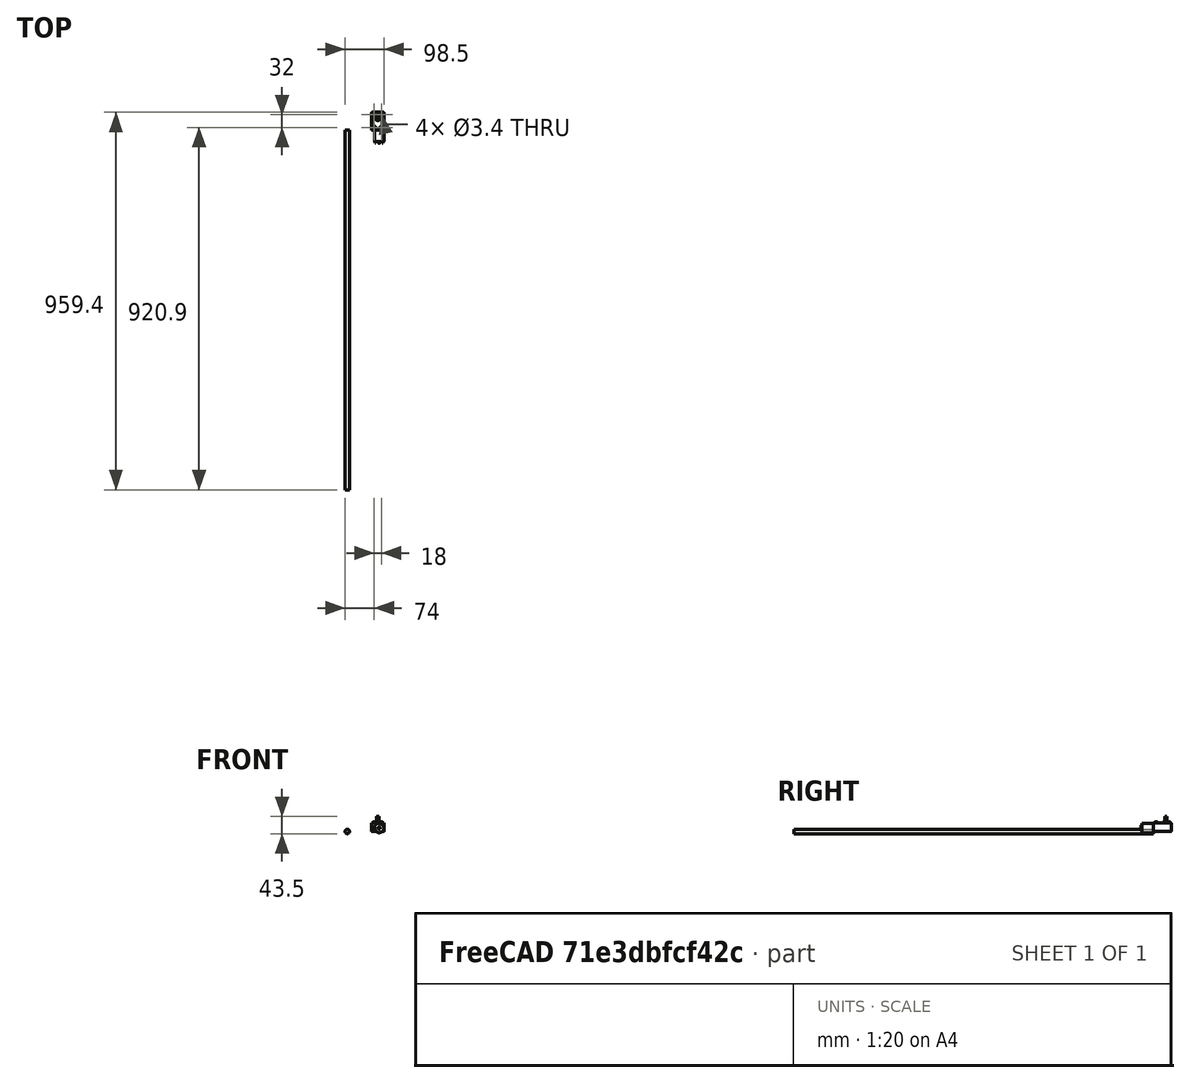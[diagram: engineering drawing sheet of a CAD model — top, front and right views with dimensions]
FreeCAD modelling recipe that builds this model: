
FCSTD DOCUMENT  (FreeCAD 1.1R20260414 (Git shallow))
Label: chainsword_master
License: All rights reserved
LicenseURL: https://en.wikipedia.org/wiki/All_rights_reserved
objects: App::Link×13, Sketcher::SketchObject×7, PartDesign::Pad×6, App::Point×5, PartDesign::Fillet×3, PartDesign::Body×2, App::FeaturePython×2, Assembly::AssemblyLink×2, PartDesign::Hole×1, PartDesign::Pocket×1, Assembly::JointGroup×1, Assembly::AssemblyObject×1
note: 49 computed .brp shape members not serialized (recipe doc carries the construction recipe); baked Part::Feature solids carry a one-line shape summary decoded from their .brp
EXTERNAL_REF file=../eletronic_parts/12v_battery.FCStd obj=Body
EXTERNAL_REF file=../eletronic_parts/spring_button.FCStd obj=Assembly
EXTERNAL_REF file=../eletronic_parts/spring_button.FCStd obj=base
EXTERNAL_REF file=../eletronic_parts/spring_button.FCStd obj=pins
EXTERNAL_REF file=../eletronic_parts/spring_button.FCStd obj=nut
EXTERNAL_REF file=../eletronic_parts/spring_button.FCStd obj=button
EXTERNAL_REF file=../eletronic_parts/dc_to_2wire.FCStd obj=Assembly
EXTERNAL_REF file=../eletronic_parts/dc_to_2wire.FCStd obj=base
EXTERNAL_REF file=../eletronic_parts/dc_to_2wire.FCStd obj=connectors
EXTERNAL_REF file=../eletronic_parts/dc_to_2wire.FCStd obj=sockets
EXTERNAL_REF file=../eletronic_parts/dc_to_2wire.FCStd obj=aux
EXTERNAL_REF file=housing.FCStd obj=Body001

FEATURE [App::Point] Origin001
  Role = Origin
FEATURE [App::Point] Origin003
  Role = Origin
FEATURE [Sketcher::SketchObject] Sketch
  ArcFitTolerance = 1e-06
  AttachmentSupport = -> [Origin002]
  ExternalTypes = [0]
  FullyConstrained = true
  MakeInternals = false
  MapMode = 5
  Placement = pos=(0,0,0) rot=(1,0,0;1.5708rad)
  _ExternalGeoVersion = 1
  sketch-geometry (1):
    g0: Circle CenterX=0 CenterY=0 CenterZ=0 NormalX=0 NormalY=0 NormalZ=1 AngleXU=0 Radius=5.5
  constraints (2):
    c: Diameter(g0) = 11
    c: Coincident(g0,g-1)
FEATURE [PartDesign::Pad] Pad
  Direction = (0,-1,2e-16)
  Length = 914.4
  Length2 = 10
  Profile = -> Sketch
  ReferenceAxis = -> Sketch [N_Axis]
  Refine = true
  SideType = 0
  Suppressed = false
  Type = 0
  Type2 = 0
FEATURE [PartDesign::Body] Body  label="threaded_rod"
  AllowCompound = false
  Group = -> [Sketch,Pad]
  Origin = -> Origin002
  Placement = pos=(133,0,0) rot=(0,0,1;0rad)
  Tip = -> Pad
FEATURE [App::Point] Origin005  label="Origin006"
  Role = Origin
FEATURE [Sketcher::SketchObject] Sketch001
  ArcFitTolerance = 1e-06
  AttachmentSupport = -> [Origin004]
  ExternalTypes = [0]
  FullyConstrained = true
  MakeInternals = false
  MapMode = 5
  _ExternalGeoVersion = 1
  sketch-geometry (4):
    g0: LineSegment StartX=0 StartY=0 StartZ=0 EndX=31 EndY=0 EndZ=0
    g1: LineSegment StartX=31 StartY=0 StartZ=0 EndX=31 EndY=45 EndZ=0
    g2: LineSegment StartX=31 StartY=45 StartZ=0 EndX=0 EndY=45 EndZ=0
    g3: LineSegment StartX=0 StartY=45 StartZ=0 EndX=0 EndY=0 EndZ=0
  constraints (11):
    c: Coincident(g0,g1)
    c: Coincident(g1,g2)
    c: Coincident(g2,g3)
    c: Coincident(g3,g0)
    c: Horizontal(g0)
    c: Horizontal(g2)
    c: Vertical(g1)
    c: Vertical(g3)
    c: Distance(g1,g3) = 31
    c: Distance(g0,g2) = 45
    c: Coincident(g0,g-1)
FEATURE [PartDesign::Pad] Pad001
  Direction = (0,0,1)
  Length = 22
  Length2 = 10
  Profile = -> Sketch001
  ReferenceAxis = -> Sketch001 [N_Axis]
  Refine = true
  SideType = 0
  Suppressed = false
  Type = 0
  Type2 = 0
FEATURE [Sketcher::SketchObject] Sketch002
  ArcFitTolerance = 1e-06
  AttachmentSupport = -> [Pad001]
  ExternalGeometry = -> [Pad001]
  ExternalTypes = [0]
  FullyConstrained = true
  MakeInternals = false
  MapMode = 5
  Placement = pos=(0,0,0) rot=(1,0,0;1.5708rad)
  _ExternalGeoVersion = 1
  sketch-geometry (1):
    g0: Circle CenterX=19 CenterY=9 CenterZ=0 NormalX=0 NormalY=0 NormalZ=1 AngleXU=0 Radius=12
  constraints (3):
    c: Diameter(g0) = 24
    c: Distance(g0,g-1) = 3
    c: Tangent(g0,g-3)
FEATURE [PartDesign::Pad] Pad002
  BaseFeature = -> Pad001
  Direction = (0,-1,2e-16)
  Length = 30
  Length2 = 10
  Profile = -> Sketch002 [Edge1]
  ReferenceAxis = -> Sketch002 [N_Axis]
  Refine = true
  SideType = 0
  Suppressed = false
  Type = 0
  Type2 = 0
FEATURE [Sketcher::SketchObject] Sketch003
  ArcFitTolerance = 1e-06
  AttachmentSupport = -> [Pad002]
  ExternalGeometry = -> [Pad002]
  ExternalTypes = [0]
  FullyConstrained = false
  MakeInternals = false
  MapMode = 5
  Placement = pos=(0,-30,0) rot=(1,0,0;1.5708rad)
  _ExternalGeoVersion = 1
  sketch-geometry (9):
    g0: LineSegment StartX=26.7462 StartY=15.1042 StartZ=0 EndX=28.7462 EndY=15.1042 EndZ=0
    g1: LineSegment StartX=28.7462 StartY=15.1042 StartZ=0 EndX=28.7462 EndY=14.9042 EndZ=0
    g2: LineSegment StartX=28.7462 StartY=14.9042 StartZ=0 EndX=26.7462 EndY=14.9042 EndZ=0
    g3: LineSegment StartX=26.7462 StartY=14.9042 StartZ=0 EndX=26.7462 EndY=15.1042 EndZ=0
    g4: LineSegment StartX=8.30695 StartY=4.56812 StartZ=0 EndX=10.307 EndY=4.56812 EndZ=0
    g5: LineSegment StartX=10.307 StartY=4.56812 StartZ=0 EndX=10.307 EndY=4.76812 EndZ=0
    g6: LineSegment StartX=10.307 StartY=4.76812 StartZ=0 EndX=8.30695 EndY=4.76812 EndZ=0
    g7: LineSegment StartX=8.30695 StartY=4.76812 StartZ=0 EndX=8.30695 EndY=4.56812 EndZ=0
    g8: Circle CenterX=19 CenterY=9 CenterZ=0 NormalX=0 NormalY=0 NormalZ=1 AngleXU=0 Radius=2.5
  constraints (24):
    c: Coincident(g0,g1)
    c: Coincident(g1,g2)
    c: Coincident(g2,g3)
    c: Coincident(g3,g0)
    c: Horizontal(g0)
    c: Horizontal(g2)
    c: Vertical(g1)
    c: Vertical(g3)
    c: Coincident(g4,g5)
    c: Coincident(g5,g6)
    c: Coincident(g6,g7)
    c: Coincident(g7,g4)
    c: Horizontal(g4)
    c: Horizontal(g6)
    c: Vertical(g5)
    c: Vertical(g7)
    c: Distance(g5,g7) = 2
    c: Distance(g4,g6) = 0.2
    c: Equal(g2,g6)
    c: Equal(g7,g3)
    c: Distance(g6,g-3) = 0.5
    c: Distance(g0,g-3) = 0.5
    c: Coincident(g8,g-3)
    c: Diameter(g8) = 5
FEATURE [PartDesign::Pad] Pad003
  BaseFeature = -> Pad002
  Direction = (0,-1,2e-16)
  Length = 3
  Length2 = 10
  Profile = -> Sketch003
  ReferenceAxis = -> Sketch003 [N_Axis]
  Refine = true
  SideType = 0
  Suppressed = false
  Type = 0
  Type2 = 0
FEATURE [PartDesign::Fillet] Fillet
  Base = -> Pad003 [Edge39]
  BaseFeature = -> Pad003
  Radius = 0.1
  Refine = true
  SupportTransform = false
  Suppressed = false
  UseAllEdges = false
FEATURE [PartDesign::Fillet] Fillet001
  Base = -> Fillet [Edge42,Edge43,Edge44,Edge40,Edge35,Edge38,Edge49,Edge45]
  BaseFeature = -> Fillet
  Radius = 1
  Refine = true
  SupportTransform = false
  Suppressed = false
  UseAllEdges = false
FEATURE [Sketcher::SketchObject] Sketch004
  ArcFitTolerance = 1e-06
  AttachmentSupport = -> [Fillet001]
  ExternalGeometry = -> [Fillet001]
  ExternalTypes = [0,0]
  FullyConstrained = true
  MakeInternals = false
  MapMode = 5
  Placement = pos=(0,0,22) rot=(0,0,1;0rad)
  _ExternalGeoVersion = 1
  sketch-geometry (5):
    g0: Circle CenterX=6.5 CenterY=6.5 CenterZ=0 NormalX=0 NormalY=0 NormalZ=1 AngleXU=0 Radius=3.5
    g1: Circle CenterX=6.5 CenterY=38.5 CenterZ=0 NormalX=0 NormalY=0 NormalZ=1 AngleXU=0 Radius=3.5
    g2: Circle CenterX=24.5 CenterY=6.5 CenterZ=0 NormalX=0 NormalY=0 NormalZ=1 AngleXU=0 Radius=3.5
    g3: Circle CenterX=24.5 CenterY=38.5 CenterZ=0 NormalX=0 NormalY=0 NormalZ=1 AngleXU=0 Radius=3.5
    g4: Circle CenterX=15.5 CenterY=30.5 CenterZ=0 NormalX=0 NormalY=0 NormalZ=1 AngleXU=0 Radius=6.5
  constraints (15):
    c: Diameter(g0) = 7
    c: Distance(g0,g-2) = 3
    c: Distance(g0,g-1) = 3
    c: Equal(g0,g1)
    c: Equal(g0,g2)
    c: Equal(g0,g3)
    c: Distance(g1,g-3) = 3
    c: Distance(g1,g-2) = 3
    c: Distance(g3,g-3) = 3
    c: Distance(g3,g-4) = 3
    c: Distance(g2,g-4) = 3
    c: Distance(g2,g-1) = 3
    c: Diameter(g4) = 13
    c: Distance(g4,g-3) = 8
    c: Distance(g4,g-2) = 9
FEATURE [PartDesign::Pad] Pad004
  BaseFeature = -> Fillet001
  Direction = (0,0,1)
  Length = 2
  Length2 = 10
  Profile = -> Sketch004
  ReferenceAxis = -> Sketch004 [N_Axis]
  Refine = true
  SideType = 0
  Suppressed = false
  Type = 0
  Type2 = 0
FEATURE [PartDesign::Hole] Hole
  BaseFeature = -> Pad004
  BaseProfileType = 7
  CustomThreadClearance = 0
  Depth = 3
  DepthType = 0
  Diameter = 3.4
  DrillForDepth = false
  DrillPoint = 1
  DrillPointAngle = 118
  HoleCutCountersinkAngle = 90
  HoleCutCustomValues = false
  HoleCutDepth = 0
  HoleCutDiameter = 0
  HoleCutType = 0
  ModelThread = false
  Profile = -> Pad004 [Face43,Face41,Face39,Face40]
  Refine = true
  Suppressed = false
  Tapered = false
  TaperedAngle = 90
  ThreadClass = 0
  ThreadDepth = 3
  ThreadDepthType = 0
  ThreadDiameter = 3
  ThreadDirection = 0
  ThreadFit = 0
  ThreadSize = 9
  ThreadType = 1
  Threaded = false
  UseCustomThreadClearance = false
FEATURE [PartDesign::Fillet] Fillet002
  Base = -> Hole [Edge80,Edge84,Edge88,Edge82,Edge86]
  BaseFeature = -> Hole
  Radius = 0.2
  Refine = true
  SupportTransform = false
  Suppressed = false
  UseAllEdges = false
FEATURE [Sketcher::SketchObject] Sketch005
  ArcFitTolerance = 1e-06
  AttachmentSupport = -> [Fillet002]
  ExternalGeometry = -> [Fillet002]
  ExternalTypes = [0]
  FullyConstrained = true
  MakeInternals = false
  MapMode = 5
  Placement = pos=(0,0,24) rot=(0,0,1;0rad)
  _ExternalGeoVersion = 1
  sketch-geometry (1):
    g0: Circle CenterX=15.5 CenterY=30.5 CenterZ=0 NormalX=0 NormalY=0 NormalZ=1 AngleXU=0 Radius=3
  constraints (2):
    c: Diameter(g0) = 6
    c: Coincident(g0,g-3)
FEATURE [PartDesign::Pad] Pad005
  BaseFeature = -> Fillet002
  Direction = (0,0,1)
  Length = 14
  Length2 = 10
  Profile = -> Sketch005
  ReferenceAxis = -> Sketch005 [N_Axis]
  Refine = true
  SideType = 0
  Suppressed = false
  Type = 0
  Type2 = 0
FEATURE [Sketcher::SketchObject] Sketch006
  ArcFitTolerance = 1e-06
  AttachmentSupport = -> [Pad005]
  ExternalGeometry = -> [Pad005]
  ExternalTypes = [0]
  FullyConstrained = false
  MakeInternals = false
  MapMode = 5
  Placement = pos=(0,0,38) rot=(0,0,1;0rad)
  _ExternalGeoVersion = 1
  sketch-geometry (4):
    g0: LineSegment StartX=14.0077 StartY=27.8975 StartZ=0 EndX=14.0077 EndY=27.0465 EndZ=0
    g1: LineSegment StartX=14.0077 StartY=27.0465 StartZ=0 EndX=17.0077 EndY=27.0465 EndZ=0
    g2: LineSegment StartX=17.0077 StartY=27.0465 StartZ=0 EndX=17.0077 EndY=27.8975 EndZ=0
    g3: LineSegment StartX=17.0077 StartY=27.8975 StartZ=0 EndX=14.0077 EndY=27.8975 EndZ=0
  constraints (10):
    c: Coincident(g0,g1)
    c: Coincident(g1,g2)
    c: Coincident(g2,g3)
    c: Coincident(g3,g0)
    c: Vertical(g0)
    c: Vertical(g2)
    c: Horizontal(g1)
    c: Horizontal(g3)
    c: PointOnObject(g0,g-3)
    c: DistanceX(g3,g3) = 3
FEATURE [PartDesign::Pocket] Pocket
  BaseFeature = -> Pad005
  Direction = (0,0,-1)
  Length = 12
  Length2 = 5
  Profile = -> Sketch006
  ReferenceAxis = -> Sketch006 [N_Axis]
  Refine = true
  SideType = 0
  Suppressed = false
  Type = 0
  Type2 = 0
FEATURE [PartDesign::Body] Body001  label="12v_DC_Motor"
  AllowCompound = true
  Group = -> [Sketch001,Pad001,Sketch002,Pad002,Sketch003,Pad003,Fillet,Fillet001,Sketch004,Pad004,Hole,Fillet002,Sketch005,Pad005,Sketch006,Pocket]
  Origin = -> Origin004
  Placement = pos=(195,0,0) rot=(0,0,1;0rad)
  Tip = -> Pocket
FEATURE [App::Link] Link
FEATURE [App::Link] threaded_rod  label="threaded_rod001"
  LinkedObject = -> Body
FEATURE [App::FeaturePython] GroundedJoint  # Assembly grounded joint (typed FeaturePython)
  ObjectToGround = -> threaded_rod
FEATURE [App::Link] _12v_DC_Motor  label="12v_DC_Motor001"
  LinkPlacement = pos=(34.2445,-236.883,-25.2543) rot=(-0.603023,-0.603023,0.603023;2.0944rad)
  LinkedObject = -> Body001
  Placement = pos=(34.2445,-236.883,-25.2543) rot=(-0.603023,-0.603023,0.603023;2.0944rad)
FEATURE [App::Link] Body002  label="Body"
  LinkPlacement = pos=(-22.0557,-193.633,-86.7561) rot=(0,0,1.04447;3.53429rad)
  LinkedObject = -> <external ../eletronic_parts/12v_battery.FCStd>#Body
  Placement = pos=(-22.0557,-193.633,-86.7561) rot=(0,0,1.04447;3.53429rad)
FEATURE [App::Point] Origin009  label="Origin011"
  Role = Origin
FEATURE [App::Link] base001  label="base002"
  LinkedObject = -> <external ../eletronic_parts/spring_button.FCStd>#base
FEATURE [App::Link] pins001  label="pins002"
  LinkPlacement = pos=(-0.25,7e-16,1) rot=(0,0,1;0rad)
  LinkedObject = -> <external ../eletronic_parts/spring_button.FCStd>#pins
  Placement = pos=(-0.25,7e-16,1) rot=(0,0,1;0rad)
FEATURE [App::Link] nut001  label="nut002"
  LinkPlacement = pos=(0,-11.7053,2.6e-15) rot=(0,0,1;0rad)
  LinkedObject = -> <external ../eletronic_parts/spring_button.FCStd>#nut
  Placement = pos=(0,-11.7053,2.6e-15) rot=(0,0,1;0rad)
FEATURE [App::Link] button001  label="button002"
  LinkPlacement = pos=(-4.8e-15,1.5,-4.6e-15) rot=(0,1,0;1.5708rad)
  LinkedObject = -> <external ../eletronic_parts/spring_button.FCStd>#button
  Placement = pos=(-4.8e-15,1.5,-4.6e-15) rot=(0,1,0;1.5708rad)
FEATURE [Assembly::AssemblyLink] Assembly002  label="button"
  Group = -> [base001,pins001,nut001,button001]
  LinkedObject = -> <external ../eletronic_parts/spring_button.FCStd>#Assembly
  Origin = -> Origin008
  Placement = pos=(-23.2078,-199.6,-0.0785183) rot=(0.999349,0,0;1.5708rad)
  Rigid = true
FEATURE [App::Point] Origin011  label="Origin013"
  Role = Origin
FEATURE [App::Link] base  label="base001"
  LinkedObject = -> <external ../eletronic_parts/dc_to_2wire.FCStd>#base
FEATURE [App::Link] connectors  label="connectors001"
  LinkPlacement = pos=(1,1,1) rot=(0,0,1;0rad)
  LinkedObject = -> <external ../eletronic_parts/dc_to_2wire.FCStd>#connectors
  Placement = pos=(1,1,1) rot=(0,0,1;0rad)
FEATURE [App::Link] sockets  label="sockets001"
  LinkPlacement = pos=(1,1,1) rot=(0,0,1;0rad)
  LinkedObject = -> <external ../eletronic_parts/dc_to_2wire.FCStd>#sockets
  Placement = pos=(1,1,1) rot=(0,0,1;0rad)
FEATURE [App::Link] aux  label="aux001"
  LinkPlacement = pos=(4e-16,-3.6e-15,-1.1e-15) rot=(0,0,1;0rad)
  LinkedObject = -> <external ../eletronic_parts/dc_to_2wire.FCStd>#aux
  Placement = pos=(4e-16,-3.6e-15,-1.1e-15) rot=(0,0,1;0rad)
FEATURE [Assembly::AssemblyLink] Assembly003  label="connector"
  Group = -> [base,connectors,sockets,aux]
  LinkedObject = -> <external ../eletronic_parts/dc_to_2wire.FCStd>#Assembly
  Origin = -> Origin010
  Placement = pos=(19.7616,-220.699,42.4752) rot=(-1.04447,0,0;1.5708rad)
  Rigid = true
FEATURE [App::Link] Body003  label="housing"
  LinkPlacement = pos=(-4.9e-15,-129.382,-39.75) rot=(0,0,1;0rad)
  LinkedObject = -> <external housing.FCStd>#Body001
  Placement = pos=(-4.9e-15,-129.382,-39.75) rot=(0,0,1;0rad)
FEATURE [App::FeaturePython] Joint  label="Slider001"  # Assembly joint (typed FeaturePython)
  Angle = 0
  AngleMax = 0
  AngleMin = 0
  Detach1 = false
  Detach2 = false
  Distance = 0
  Distance2 = 0
  EnableAngleMax = false
  EnableAngleMin = false
  EnableLengthMax = false
  EnableLengthMin = false
  JointType = 3 (Slider)
  LengthMax = 0
  LengthMin = 0
  Offset2 = pos=(0,0,0) rot=(0,0,1;3.14159rad)
  Placement1 = pos=(40,-61,-55) rot=(1,0,0;1.5708rad)
  Placement2 = pos=(0,0,0) rot=(0,-0.707107,0.707107;3.14159rad)
  Reference1 = -> Body003 [?Face20,?Face20]
  Reference2 = -> threaded_rod [Face1,Edge2]
  Suppressed = false
FEATURE [Assembly::JointGroup] Joints
  Group = -> [GroundedJoint,Joint]
FEATURE [Assembly::AssemblyObject] Assembly
  Group = -> [Joints,Link,threaded_rod,GroundedJoint,_12v_DC_Motor,Body002,Assembly002,Assembly003,Body003,Joint]
  Origin = -> Origin
  Type = Assembly

RESOLVED EXTERNAL PARTS (link-assembly join: the EXTERNAL_REF files above that resolve inside this repo's crawl, each included once):
---- part ../eletronic_parts/12v_battery.FCStd = doc fcstd_0e6d6dc54b79 ----
FCSTD DOCUMENT  (FreeCAD 1.1R20260414 (Git shallow))
Label: 12v_battery
License: All rights reserved
LicenseURL: https://en.wikipedia.org/wiki/All_rights_reserved
objects: Sketcher::SketchObject×2, PartDesign::Pad×2, App::Point×1, PartDesign::Fillet×1, PartDesign::Body×1
note: 14 computed .brp shape members not serialized (recipe doc carries the construction recipe); baked Part::Feature solids carry a one-line shape summary decoded from their .brp

FEATURE [App::Point] Origin001
  Role = Origin
FEATURE [Sketcher::SketchObject] Sketch
  ArcFitTolerance = 1e-06
  AttachmentSupport = -> [Origin]
  ExternalTypes = [0]
  FullyConstrained = true
  MakeInternals = false
  MapMode = 5
  _ExternalGeoVersion = 1
  sketch-geometry (4):
    g0: LineSegment StartX=23.094 StartY=0 StartZ=0 EndX=-11.547 EndY=20 EndZ=0
    g1: LineSegment StartX=-11.547 StartY=20 StartZ=0 EndX=-11.547 EndY=-20 EndZ=0
    g2: LineSegment StartX=-11.547 StartY=-20 StartZ=0 EndX=23.094 EndY=0 EndZ=0
    g3: Circle [constr] CenterX=0 CenterY=0 CenterZ=0 NormalX=0 NormalY=0 NormalZ=1 AngleXU=0 Radius=23.094
  constraints (11):
    c: Coincident(g0,g1)
    c: Coincident(g1,g2)
    c: Coincident(g2,g0)
    c: Equal(g0,g1)
    c: Equal(g0,g2)
    c: PointOnObject(g0,g3)
    c: PointOnObject(g1,g3)
    c: PointOnObject(g2,g3)
    c: Coincident(g3,g-1)
    c: PointOnObject(g2,g-1)
    c: Distance(g0,g0) = 40
FEATURE [PartDesign::Pad] Pad
  Direction = (0,0,1)
  Length = 62
  Length2 = 10
  Profile = -> Sketch
  ReferenceAxis = -> Sketch [N_Axis]
  Refine = true
  SideType = 0
  Suppressed = false
  Type = 0
  Type2 = 0
FEATURE [PartDesign::Fillet] Fillet
  Base = -> Pad [Edge2,Edge1,Edge5]
  BaseFeature = -> Pad
  Radius = 1
  Refine = true
  SupportTransform = false
  Suppressed = false
  UseAllEdges = false
FEATURE [Sketcher::SketchObject] Sketch001
  ArcFitTolerance = 1e-06
  AttachmentSupport = -> [Fillet]
  ExternalGeometry = -> [Fillet]
  ExternalTypes = [0]
  FullyConstrained = true
  MakeInternals = false
  MapMode = 5
  Placement = pos=(0,0,62) rot=(0,0,1;0rad)
  _ExternalGeoVersion = 1
  sketch-geometry (4):
    g0: LineSegment StartX=-11.547 StartY=5.5 StartZ=0 EndX=-11.547 EndY=-5.5 EndZ=0
    g1: LineSegment StartX=-11.547 StartY=-5.5 StartZ=0 EndX=-1.54701 EndY=-5.5 EndZ=0
    g2: LineSegment StartX=-1.54701 StartY=-5.5 StartZ=0 EndX=-1.54701 EndY=5.5 EndZ=0
    g3: LineSegment StartX=-1.54701 StartY=5.5 StartZ=0 EndX=-11.547 EndY=5.5 EndZ=0
  constraints (12):
    c: Coincident(g0,g1)
    c: Coincident(g1,g2)
    c: Coincident(g2,g3)
    c: Coincident(g3,g0)
    c: Vertical(g0)
    c: Vertical(g2)
    c: Horizontal(g1)
    c: Horizontal(g3)
    c: PointOnObject(g0,g-3)
    c: DistanceX(g3,g3) = 10
    c: DistanceY(g0,g0) = 11
    c: Distance(g-1,g3) = 5.5
FEATURE [PartDesign::Pad] Pad001
  BaseFeature = -> Fillet
  Direction = (0,0,1)
  Length = 5
  Length2 = 10
  Profile = -> Sketch001
  ReferenceAxis = -> Sketch001 [N_Axis]
  Refine = true
  SideType = 0
  Suppressed = false
  Type = 0
  Type2 = 0
FEATURE [PartDesign::Body] Body
  AllowCompound = true
  Group = -> [Sketch,Pad,Fillet,Sketch001,Pad001]
  Origin = -> Origin
  Tip = -> Pad001
---- part ../eletronic_parts/dc_to_2wire.FCStd = doc fcstd_c95eb83013e7 ----
FCSTD DOCUMENT  (FreeCAD 1.1R20260414 (Git shallow))
Label: dc_to_2wire
License: All rights reserved
LicenseURL: https://en.wikipedia.org/wiki/All_rights_reserved
objects: Sketcher::SketchObject×9, PartDesign::Pad×7, App::Point×5, PartDesign::Plane×5, PartDesign::Body×4, App::Link×4, App::FeaturePython×4, PartDesign::Fillet×2, PartDesign::Mirrored×2, PartDesign::AdditiveLoft×1, PartDesign::SubtractivePipe×1, Assembly::JointGroup×1, Assembly::AssemblyObject×1
note: 64 computed .brp shape members not serialized (recipe doc carries the construction recipe); baked Part::Feature solids carry a one-line shape summary decoded from their .brp

FEATURE [App::Point] Origin001
  Role = Origin
FEATURE [Sketcher::SketchObject] Sketch
  ArcFitTolerance = 1e-06
  AttachmentSupport = -> [Origin]
  ExternalTypes = [0]
  FullyConstrained = true
  MakeInternals = false
  MapMode = 5
  Placement = pos=(0,0,0) rot=(1,0,0;1.5708rad)
  _ExternalGeoVersion = 1
  sketch-geometry (10):
    g0: LineSegment StartX=-6 StartY=-6 StartZ=0 EndX=6 EndY=-6 EndZ=0
    g1: LineSegment StartX=7 StartY=-5 StartZ=0 EndX=7 EndY=5 EndZ=0
    g2: LineSegment StartX=6 StartY=6 StartZ=0 EndX=-6 EndY=6 EndZ=0
    g3: LineSegment StartX=-7 StartY=5 StartZ=0 EndX=-7 EndY=-5 EndZ=0
    g4: ArcOfCircle CenterX=-6 CenterY=-5 CenterZ=0 NormalX=0 NormalY=0 NormalZ=1 AngleXU=0 Radius=1 StartAngle=3.14159 EndAngle=4.71239
    g5: ArcOfCircle CenterX=6 CenterY=-5 CenterZ=0 NormalX=0 NormalY=0 NormalZ=1 AngleXU=0 Radius=1 StartAngle=4.71239 EndAngle=6.28319
    g6: ArcOfCircle CenterX=6 CenterY=5 CenterZ=0 NormalX=0 NormalY=0 NormalZ=1 AngleXU=0 Radius=1 StartAngle=0 EndAngle=1.5708
    g7: ArcOfCircle CenterX=-6 CenterY=5 CenterZ=0 NormalX=0 NormalY=0 NormalZ=1 AngleXU=0 Radius=1 StartAngle=1.5708 EndAngle=3.14159
    g8: GeomPoint [constr] X=7 Y=6 Z=0
    g9: GeomPoint [constr] X=-2.33e-14 Y=2.6e-14 Z=0
  constraints (22):
    c: Tangent(g0,g4) = -1.5708
    c: Tangent(g0,g5) = -1.5708
    c: Tangent(g1,g5) = -1.5708
    c: Tangent(g1,g6) = -1.5708
    c: Tangent(g2,g6) = -1.5708
    c: Tangent(g2,g7) = -1.5708
    c: Tangent(g3,g7) = -1.5708
    c: Tangent(g3,g4) = -1.5708
    c: Horizontal(g0)
    c: Horizontal(g2)
    c: Vertical(g1)
    c: Vertical(g3)
    c: Equal(g4,g5)
    c: Equal(g5,g6)
    c: Equal(g6,g7)
    c: Symmetric(g2,g0,g9)
    c: PointOnObject(g8,g1)
    c: PointOnObject(g8,g2)
    c: Distance(g1,g3) = 14
    c: Distance(g0,g2) = 12
    c: Radius(g5) = 1
    c: Coincident(g9,g-1)
FEATURE [PartDesign::Pad] Pad
  Direction = (0,-1,2e-16)
  Length = 12
  Length2 = 10
  Profile = -> Sketch
  ReferenceAxis = -> Sketch [N_Axis]
  Refine = true
  SideType = 0
  Suppressed = false
  Type = 0
  Type2 = 0
FEATURE [PartDesign::Plane] DatumPlane
  AttachmentOffset = pos=(0,0,10) rot=(0,0,1;0rad)
  AttachmentSupport = -> [Pad]
  Length = 60
  MapMode = 5
  Placement = pos=(0,-22,2.2e-15) rot=(1,0,0;1.5708rad)
  ResizeMode = 0
  Width = 60
FEATURE [Sketcher::SketchObject] Sketch001
  ArcFitTolerance = 1e-06
  AttachmentSupport = -> [DatumPlane]
  ExternalTypes = [0]
  FullyConstrained = true
  MakeInternals = false
  MapMode = 5
  Placement = pos=(0,-22,2.2e-15) rot=(1,0,0;1.5708rad)
  _ExternalGeoVersion = 1
  sketch-geometry (10):
    g0: LineSegment StartX=-5 StartY=-5.5 StartZ=0 EndX=5 EndY=-5.5 EndZ=0
    g1: LineSegment StartX=6 StartY=-4.5 StartZ=0 EndX=6 EndY=4.5 EndZ=0
    g2: LineSegment StartX=5 StartY=5.5 StartZ=0 EndX=-5 EndY=5.5 EndZ=0
    g3: LineSegment StartX=-6 StartY=4.5 StartZ=0 EndX=-6 EndY=-4.5 EndZ=0
    g4: ArcOfCircle CenterX=-5 CenterY=-4.5 CenterZ=0 NormalX=0 NormalY=0 NormalZ=1 AngleXU=0 Radius=1 StartAngle=3.14159 EndAngle=4.71239
    g5: ArcOfCircle CenterX=5 CenterY=-4.5 CenterZ=0 NormalX=0 NormalY=0 NormalZ=1 AngleXU=0 Radius=1 StartAngle=4.71239 EndAngle=6.28319
    g6: ArcOfCircle CenterX=5 CenterY=4.5 CenterZ=0 NormalX=0 NormalY=0 NormalZ=1 AngleXU=0 Radius=1 StartAngle=0 EndAngle=1.5708
    g7: ArcOfCircle CenterX=-5 CenterY=4.5 CenterZ=0 NormalX=0 NormalY=0 NormalZ=1 AngleXU=0 Radius=1 StartAngle=1.5708 EndAngle=3.14159
    g8: GeomPoint [constr] X=6 Y=5.5 Z=0
    g9: GeomPoint [constr] X=0 Y=1.17e-14 Z=0
  constraints (22):
    c: Tangent(g0,g4) = -1.5708
    c: Tangent(g0,g5) = -1.5708
    c: Tangent(g1,g5) = -1.5708
    c: Tangent(g1,g6) = -1.5708
    c: Tangent(g2,g6) = -1.5708
    c: Tangent(g2,g7) = -1.5708
    c: Tangent(g3,g7) = -1.5708
    c: Tangent(g3,g4) = -1.5708
    c: Horizontal(g0)
    c: Horizontal(g2)
    c: Vertical(g1)
    c: Vertical(g3)
    c: Equal(g4,g5)
    c: Equal(g5,g6)
    c: Equal(g6,g7)
    c: Symmetric(g2,g0,g9)
    c: PointOnObject(g8,g1)
    c: PointOnObject(g8,g2)
    c: Distance(g1,g3) = 12
    c: Distance(g0,g2) = 11
    c: Radius(g5) = 1
    c: Coincident(g9,g-1)
FEATURE [PartDesign::AdditiveLoft] AdditiveLoft
  BaseFeature = -> Pad
  Closed = false
  Profile = -> Pad [Face10]
  Refine = true
  Ruled = false
  Sections = -> [Sketch001]
  Suppressed = false
FEATURE [Sketcher::SketchObject] Sketch002
  ArcFitTolerance = 1e-06
  AttachmentSupport = -> [AdditiveLoft]
  ExternalTypes = [0]
  FullyConstrained = true
  MakeInternals = false
  MapMode = 5
  Placement = pos=(0,-22,0) rot=(1,0,0;1.5708rad)
  _ExternalGeoVersion = 1
  sketch-geometry (1):
    g0: Circle CenterX=0 CenterY=0 CenterZ=0 NormalX=0 NormalY=0 NormalZ=1 AngleXU=0 Radius=5
  constraints (2):
    c: Diameter(g0) = 10
    c: Coincident(g0,g-1)
FEATURE [PartDesign::Pad] Pad001
  BaseFeature = -> AdditiveLoft
  Direction = (0,-1,2e-16)
  Length = 6
  Length2 = 10
  Profile = -> Sketch002
  ReferenceAxis = -> Sketch002 [N_Axis]
  Refine = true
  SideType = 0
  Suppressed = false
  Type = 0
  Type2 = 0
FEATURE [PartDesign::Fillet] Fillet
  Base = -> Pad001 [Edge55]
  BaseFeature = -> Pad001
  Radius = 1
  Refine = true
  SupportTransform = false
  Suppressed = false
  UseAllEdges = false
FEATURE [Sketcher::SketchObject] Sketch003
  ArcFitTolerance = 1e-06
  AttachmentSupport = -> [Origin]
  ExternalGeometry = -> [Fillet]
  ExternalTypes = [0]
  FullyConstrained = false
  MakeInternals = false
  MapMode = 5
  Placement = pos=(0,0,0) rot=(0.57735,0.57735,0.57735;2.0944rad)
  _ExternalGeoVersion = 1
  sketch-geometry (24):
    g0: LineSegment StartX=-13 StartY=6.5 StartZ=0 EndX=-14 EndY=6.5 EndZ=0
    g1: LineSegment StartX=-14 StartY=6.5 StartZ=0 EndX=-14 EndY=5.5 EndZ=0
    g2: LineSegment StartX=-14 StartY=5.5 StartZ=0 EndX=-13 EndY=5.5 EndZ=0
    g3: LineSegment StartX=-13 StartY=5.5 StartZ=0 EndX=-13 EndY=6.5 EndZ=0
    g4: LineSegment StartX=-14.4641 StartY=6.45747 StartZ=0 EndX=-15.4641 EndY=6.45747 EndZ=0
    g5: LineSegment StartX=-15.4641 StartY=6.45747 StartZ=0 EndX=-15.4641 EndY=5.3215 EndZ=0
    g6: LineSegment StartX=-15.4641 StartY=5.3215 StartZ=0 EndX=-14.4641 EndY=5.3215 EndZ=0
    g7: LineSegment StartX=-14.4641 StartY=5.3215 StartZ=0 EndX=-14.4641 EndY=6.45747 EndZ=0
    g8: LineSegment StartX=-15.9959 StartY=6.24299 StartZ=0 EndX=-16.9959 EndY=6.24299 EndZ=0
    g9: LineSegment StartX=-16.9959 StartY=6.24299 StartZ=0 EndX=-16.9959 EndY=5.24299 EndZ=0
    g10: LineSegment StartX=-16.9959 StartY=5.24299 StartZ=0 EndX=-15.9959 EndY=5.24299 EndZ=0
    g11: LineSegment StartX=-15.9959 StartY=5.24299 StartZ=0 EndX=-15.9959 EndY=6.24299 EndZ=0
    g12: LineSegment StartX=-17.4938 StartY=6.16449 StartZ=0 EndX=-18.4938 EndY=6.16449 EndZ=0
    g13: LineSegment StartX=-18.4938 StartY=6.16449 StartZ=0 EndX=-18.4938 EndY=5.16449 EndZ=0
    g14: LineSegment StartX=-18.4938 StartY=5.16449 StartZ=0 EndX=-17.4938 EndY=5.16449 EndZ=0
    g15: LineSegment StartX=-17.4938 StartY=5.16449 StartZ=0 EndX=-17.4938 EndY=6.16449 EndZ=0
    g16: LineSegment StartX=-18.9918 StartY=6.08598 StartZ=0 EndX=-19.9918 EndY=6.08598 EndZ=0
    g17: LineSegment StartX=-19.9918 StartY=6.08598 StartZ=0 EndX=-19.9918 EndY=5.08598 EndZ=0
    g18: LineSegment StartX=-19.9918 StartY=5.08598 StartZ=0 EndX=-18.9918 EndY=5.08598 EndZ=0
    g19: LineSegment StartX=-18.9918 StartY=5.08598 StartZ=0 EndX=-18.9918 EndY=6.08598 EndZ=0
    g20: LineSegment StartX=-20.4897 StartY=6.00748 StartZ=0 EndX=-21.4897 EndY=6.00748 EndZ=0
    g21: LineSegment StartX=-21.4897 StartY=6.00748 StartZ=0 EndX=-21.4897 EndY=5.00748 EndZ=0
    g22: LineSegment StartX=-21.4897 StartY=5.00748 StartZ=0 EndX=-20.4897 EndY=5.00748 EndZ=0
    g23: LineSegment StartX=-20.4897 StartY=5.00748 StartZ=0 EndX=-20.4897 EndY=6.00748 EndZ=0
  constraints (52):
    c: Coincident(g0,g1)
    c: Coincident(g1,g2)
    c: Coincident(g2,g3)
    c: Coincident(g3,g0)
    c: Horizontal(g0)
    c: Horizontal(g2)
    c: Vertical(g1)
    c: Vertical(g3)
    c: Distance(g1,g3) = 1
    c: Distance(g0,g2) = 1
    c: Distance(g-3,g3) = 1
    c: DistanceY(g-3,g0) = 0.5
    c: Coincident(g4,g5)
    c: Coincident(g8,g9)
    c: Coincident(g12,g13)
    c: Coincident(g16,g17)
    c: Coincident(g20,g21)
    c: Coincident(g5,g6)
    c: Coincident(g9,g10)
    c: Coincident(g13,g14)
    c: Coincident(g17,g18)
    c: Coincident(g21,g22)
    c: Coincident(g6,g7)
    c: Coincident(g10,g11)
    c: Coincident(g14,g15)
    c: Coincident(g18,g19)
    c: Coincident(g22,g23)
    c: Coincident(g7,g4)
    c: Coincident(g11,g8)
    c: Coincident(g15,g12)
    c: Coincident(g19,g16)
    c: Coincident(g23,g20)
    c: Horizontal(g4)
    c: Horizontal(g8)
    c: Horizontal(g12)
    c: Horizontal(g16)
    c: Horizontal(g20)
    c: Horizontal(g6)
    c: Horizontal(g10)
    c: Horizontal(g14)
    c: Horizontal(g18)
    c: Horizontal(g22)
    c: Vertical(g5)
    c: Vertical(g9)
    c: Vertical(g13)
    c: Vertical(g17)
    c: Vertical(g21)
    c: Vertical(g7)
    c: Vertical(g11)
    c: Vertical(g15)
    c: Vertical(g19)
    c: Vertical(g23)
FEATURE [PartDesign::SubtractivePipe] SubtractivePipe
  AuxiliaryCurvilinear = true
  AuxiliarySpineTangent = false
  BaseFeature = -> Fillet
  Binormal = (0,0,0)
  Mode = 0
  Profile = -> Sketch003
  Refine = true
  Spine = -> Fillet [Edge17,Edge16,Edge14,Edge12,Edge10,Edge8,Edge6,Edge7,Edge9,Edge11,Edge13,Edge15]
  SpineTangent = false
  Suppressed = false
  Transformation = 0
  Transition = 0
FEATURE [PartDesign::Body] Body  label="base"
  AllowCompound = true
  Group = -> [Sketch,Pad,DatumPlane,Sketch001,AdditiveLoft,Sketch002,Pad001,Fillet,Sketch003,SubtractivePipe]
  Origin = -> Origin
  Tip = -> SubtractivePipe
FEATURE [App::Point] Origin005  label="Origin006"
  Role = Origin
FEATURE [PartDesign::Plane] DatumPlane001
  Length = 60
  MapMode = 5
  Placement = pos=(0,1.3e-15,6) rot=(0,0,1;0rad)
  ResizeMode = 0
  Width = 60
FEATURE [Sketcher::SketchObject] Sketch006
  ArcFitTolerance = 1e-06
  AttachmentSupport = -> [DatumPlane001]
  ExternalTypes = [0]
  FullyConstrained = true
  MakeInternals = false
  MapMode = 5
  Placement = pos=(0,1.3e-15,6) rot=(0,0,1;0rad)
  _ExternalGeoVersion = 1
  sketch-geometry (5):
    g0: LineSegment StartX=-5 StartY=-2 StartZ=0 EndX=5 EndY=-2 EndZ=0
    g1: LineSegment StartX=5 StartY=-2 StartZ=0 EndX=5 EndY=3 EndZ=0
    g2: LineSegment StartX=5 StartY=3 StartZ=0 EndX=-5 EndY=3 EndZ=0
    g3: LineSegment StartX=-5 StartY=3 StartZ=0 EndX=-5 EndY=-2 EndZ=0
    g4: GeomPoint [constr] X=0 Y=0.5 Z=0
  constraints (13):
    c: Coincident(g0,g1)
    c: Coincident(g1,g2)
    c: Coincident(g2,g3)
    c: Coincident(g3,g0)
    c: Horizontal(g0)
    c: Horizontal(g2)
    c: Vertical(g1)
    c: Vertical(g3)
    c: Symmetric(g2,g0,g4)
    c: Distance(g1,g3) = 10
    c: Distance(g0,g2) = 5
    c: PointOnObject(g4,g-2)
    c: Distance(g-1,g0) = 2
FEATURE [PartDesign::Pad] Pad004
  Direction = (0,0,1)
  Length = 2
  Length2 = 10
  Placement = pos=(0,1.3e-15,6) rot=(0,0,1;0rad)
  Profile = -> Sketch006
  ReferenceAxis = -> Sketch006 [N_Axis]
  Refine = true
  SideType = 1
  Suppressed = false
  Type = 0
  Type2 = 0
FEATURE [PartDesign::Body] Body002  label="sockets"
  AllowCompound = true
  Group = -> [DatumPlane001,Sketch006,Pad004]
  Origin = -> Origin004
  Tip = -> Pad004
FEATURE [App::Point] Origin007  label="Origin009"
  Role = Origin
FEATURE [PartDesign::Plane] DatumPlane002
  AttachmentSupport = -> [Pad004]
  Length = 60
  MapMode = 5
  Placement = pos=(0,3,6) rot=(0,0.707107,0.707107;3.14159rad)
  ResizeMode = 0
  Width = 60
FEATURE [Sketcher::SketchObject] Sketch007
  ArcFitTolerance = 1e-06
  AttachmentSupport = -> [DatumPlane002]
  ExternalTypes = [0]
  FullyConstrained = true
  MakeInternals = false
  MapMode = 5
  Placement = pos=(0,3,6) rot=(0,0.707107,0.707107;3.14159rad)
  _ExternalGeoVersion = 1
  sketch-geometry (4):
    g0: LineSegment StartX=0.5 StartY=-4 StartZ=0 EndX=0.5 EndY=-9 EndZ=0
    g1: LineSegment StartX=0.5 StartY=-9 StartZ=0 EndX=4.5 EndY=-9 EndZ=0
    g2: LineSegment StartX=4.5 StartY=-9 StartZ=0 EndX=4.5 EndY=-4 EndZ=0
    g3: LineSegment StartX=4.5 StartY=-4 StartZ=0 EndX=0.5 EndY=-4 EndZ=0
  constraints (12):
    c: Coincident(g0,g1)
    c: Coincident(g1,g2)
    c: Coincident(g2,g3)
    c: Coincident(g3,g0)
    c: Vertical(g0)
    c: Vertical(g2)
    c: Horizontal(g1)
    c: Horizontal(g3)
    c: Distance(g0,g2) = 4
    c: Distance(g1,g3) = 5
    c: Distance(g-2,g0) = 0.5
    c: Distance(g-1,g3) = 4
FEATURE [PartDesign::Pad] Pad005
  Direction = (0,1,-2e-16)
  Length = 0.1
  Length2 = 10
  Placement = pos=(0,3,6) rot=(0,0.707107,0.707107;3.14159rad)
  Profile = -> Sketch007
  ReferenceAxis = -> Sketch007 [N_Axis]
  Refine = true
  SideType = 0
  Suppressed = false
  Type = 0
  Type2 = 0
FEATURE [PartDesign::Mirrored] Mirrored
  BaseFeature = -> Pad005
  MirrorPlane = -> Sketch007 [V_Axis]
  Originals = -> [Pad005]
  Placement = pos=(0,3,6) rot=(0,0.707107,0.707107;3.14159rad)
  Refine = true
  Suppressed = false
  TransformMode = 0
FEATURE [PartDesign::Plane] DatumPlane003
  AttachmentSupport = -> [Pad004]
  Length = 60
  MapMode = 5
  Placement = pos=(0,1.3e-15,8) rot=(0,0,1;0rad)
  ResizeMode = 0
  Width = 60
FEATURE [Sketcher::SketchObject] Sketch008
  ArcFitTolerance = 1e-06
  AttachmentSupport = -> [DatumPlane003]
  ExternalTypes = [0]
  FullyConstrained = true
  MakeInternals = false
  MapMode = 5
  Placement = pos=(0,1.3e-15,8) rot=(0,0,1;0rad)
  _ExternalGeoVersion = 1
  sketch-geometry (1):
    g0: Circle CenterX=-2.5 CenterY=1 CenterZ=0 NormalX=0 NormalY=0 NormalZ=1 AngleXU=0 Radius=1.5
  constraints (3):
    c: Diameter(g0) = 3
    c: Distance(g0,g-2) = 1
    c: Distance(g0,g-1) = 1
FEATURE [PartDesign::Pad] Pad006
  BaseFeature = -> Mirrored
  Direction = (0,0,1)
  Length = 0.1
  Length2 = 10
  Placement = pos=(0,3,6) rot=(0,0.707107,0.707107;3.14159rad)
  Profile = -> Sketch008
  ReferenceAxis = -> Sketch008 [N_Axis]
  Refine = true
  SideType = 0
  Suppressed = false
  Type = 0
  Type2 = 0
FEATURE [PartDesign::Mirrored] Mirrored001
  BaseFeature = -> Pad006
  MirrorPlane = -> Sketch008 [V_Axis]
  Originals = -> [Pad006]
  Placement = pos=(0,3,6) rot=(0,0.707107,0.707107;3.14159rad)
  Refine = true
  Suppressed = false
  TransformMode = 0
FEATURE [PartDesign::Body] Body003  label="connectors"
  AllowCompound = true
  Group = -> [DatumPlane002,Sketch007,Pad005,Mirrored,DatumPlane003,Sketch008,Pad006,Mirrored001]
  Origin = -> Origin006
  Tip = -> Mirrored001
FEATURE [App::Point] Origin009  label="Origin011"
  Role = Origin
FEATURE [PartDesign::Plane] DatumPlane004
  AttachmentSupport = -> [SubtractivePipe]
  Length = 60
  MapMode = 5
  Placement = pos=(0,-28,0) rot=(1,0,0;1.5708rad)
  ResizeMode = 0
  Width = 60
FEATURE [Sketcher::SketchObject] Sketch009
  ArcFitTolerance = 1e-06
  AttachmentSupport = -> [DatumPlane004]
  ExternalTypes = [0]
  FullyConstrained = true
  MakeInternals = false
  MapMode = 5
  Placement = pos=(0,-28,0) rot=(1,0,0;1.5708rad)
  _ExternalGeoVersion = 1
  sketch-geometry (2):
    g0: Circle CenterX=0 CenterY=0 CenterZ=0 NormalX=0 NormalY=0 NormalZ=1 AngleXU=0 Radius=3.5
    g1: Circle CenterX=0 CenterY=0 CenterZ=0 NormalX=0 NormalY=0 NormalZ=1 AngleXU=0 Radius=3.3
  constraints (4):
    c: Diameter(g0) = 7
    c: Coincident(g0,g-1)
    c: Coincident(g1,g0)
    c: Distance(g1,g0) = 0.2
FEATURE [PartDesign::Pad] Pad007
  Direction = (0,-1,2e-16)
  Length = 3
  Length2 = 10
  Placement = pos=(0,-28,0) rot=(1,0,0;1.5708rad)
  Profile = -> Sketch009
  ReferenceAxis = -> Sketch009 [N_Axis]
  Refine = true
  SideType = 0
  Suppressed = false
  TaperAngle = -4
  Type = 0
  Type2 = 0
FEATURE [Sketcher::SketchObject] Sketch010
  ArcFitTolerance = 1e-06
  AttachmentSupport = -> [DatumPlane004]
  ExternalTypes = [0]
  FullyConstrained = true
  MakeInternals = false
  MapMode = 5
  Placement = pos=(0,-28,0) rot=(1,0,0;1.5708rad)
  _ExternalGeoVersion = 1
  sketch-geometry (1):
    g0: Circle CenterX=0 CenterY=0 CenterZ=0 NormalX=0 NormalY=0 NormalZ=1 AngleXU=0 Radius=1
  constraints (2):
    c: Diameter(g0) = 2
    c: Coincident(g0,g-1)
FEATURE [PartDesign::Pad] Pad008
  BaseFeature = -> Pad007
  Direction = (0,-1,2e-16)
  Length = 2.5
  Length2 = 10
  Placement = pos=(0,-28,0) rot=(1,0,0;1.5708rad)
  Profile = -> Sketch010
  ReferenceAxis = -> Sketch010 [N_Axis]
  Refine = true
  SideType = 0
  Suppressed = false
  Type = 0
  Type2 = 0
FEATURE [PartDesign::Fillet] Fillet001
  Base = -> Pad008 [Edge9]
  BaseFeature = -> Pad008
  Placement = pos=(0,-28,0) rot=(1,0,0;1.5708rad)
  Radius = 1
  Refine = true
  SupportTransform = false
  Suppressed = false
  UseAllEdges = false
FEATURE [PartDesign::Body] Body004  label="aux"
  AllowCompound = true
  Group = -> [DatumPlane004,Sketch009,Pad007,Sketch010,Pad008,Fillet001]
  Origin = -> Origin008
  Tip = -> Fillet001
FEATURE [App::Point] Origin011  label="Origin014"
  Role = Origin
FEATURE [App::Link] base  label="base001"
  LinkedObject = -> Body
FEATURE [App::FeaturePython] GroundedJoint  # Assembly grounded joint (typed FeaturePython)
  ObjectToGround = -> base
FEATURE [App::Link] connectors  label="connectors001"
  LinkPlacement = pos=(1,1,1) rot=(0,0,1;0rad)
  LinkedObject = -> Body003
  Placement = pos=(1,1,1) rot=(0,0,1;0rad)
FEATURE [App::Link] sockets  label="sockets001"
  LinkPlacement = pos=(1,1,1) rot=(0,0,1;0rad)
  LinkedObject = -> Body002
  Placement = pos=(1,1,1) rot=(0,0,1;0rad)
FEATURE [App::Link] aux  label="aux001"
  LinkPlacement = pos=(4e-16,-3.6e-15,-1.1e-15) rot=(0,0,1;0rad)
  LinkedObject = -> Body004
  Placement = pos=(4e-16,-3.6e-15,-1.1e-15) rot=(0,0,1;0rad)
FEATURE [App::FeaturePython] Joint  label="Fixed"  # Assembly joint (typed FeaturePython)
  Angle = 0
  AngleMax = 0
  AngleMin = 0
  Detach1 = false
  Detach2 = false
  Distance = 0
  Distance2 = 0
  EnableAngleMax = false
  EnableAngleMin = false
  EnableLengthMax = false
  EnableLengthMin = false
  JointType = 0 (Fixed)
  LengthMax = 0
  LengthMin = 0
  Placement1 = pos=(0,-28,1e-15) rot=(0.57735,0.57735,0.57735;4.18879rad)
  Placement2 = pos=(4e-16,-28,-1e-16) rot=(0.57735,0.57735,0.57735;4.18879rad)
  Reference1 = -> aux [Face3,Edge1]
  Reference2 = -> base [Face95,Face95]
  Suppressed = false
FEATURE [App::FeaturePython] Joint001  label="Fixed008"  # Assembly joint (typed FeaturePython)
  Angle = 0
  AngleMax = 0
  AngleMin = 0
  Detach1 = false
  Detach2 = false
  Distance = 0
  Distance2 = 0
  EnableAngleMax = false
  EnableAngleMin = false
  EnableLengthMax = false
  EnableLengthMin = false
  JointType = 0 (Fixed)
  LengthMax = 0
  LengthMin = 0
  Offset1 = pos=(0,0.5,0) rot=(0,0,1;0rad)
  Offset2 = pos=(0,0,0) rot=(0,0,1;1.5708rad)
  Placement1 = pos=(-9e-16,3,2) rot=(0.57735,-0.57735,0.57735;2.0944rad)
  Placement2 = pos=(0,3,2) rot=(0.57735,0.57735,0.57735;4.18879rad)
  Reference1 = -> connectors [Face11,Vertex9]
  Reference2 = -> sockets [Face3,Face3]
  Suppressed = false
FEATURE [App::FeaturePython] Joint002  label="Fixed010"  # Assembly joint (typed FeaturePython)
  Angle = 0
  AngleMax = 0
  AngleMin = 0
  Detach1 = false
  Detach2 = false
  Distance = 0
  Distance2 = 0
  EnableAngleMax = false
  EnableAngleMin = false
  EnableLengthMax = false
  EnableLengthMin = false
  JointType = 0 (Fixed)
  LengthMax = 0
  LengthMin = 0
  Offset2 = pos=(3,1,-1) rot=(0,0,1;1.5708rad)
  Placement1 = pos=(1e-16,-2,2) rot=(1,0,0;1.5708rad)
  Placement2 = pos=(1,-1,3) rot=(1,0,0;4.71239rad)
  Reference1 = -> sockets [Face1,Face1]
  Reference2 = -> base [Face25,Face25]
  Suppressed = false
FEATURE [Assembly::JointGroup] Joints
  Group = -> [GroundedJoint,Joint,Joint001,Joint002]
FEATURE [Assembly::AssemblyObject] Assembly
  Group = -> [Joints,base,GroundedJoint,connectors,sockets,aux,Joint,Joint001,Joint002]
  Origin = -> Origin010
  Type = Assembly
---- part ../eletronic_parts/spring_button.FCStd = doc fcstd_6cd288684a3d ----
FCSTD DOCUMENT  (FreeCAD 1.1R20260414 (Git shallow))
Label: spring_button
License: All rights reserved
LicenseURL: https://en.wikipedia.org/wiki/All_rights_reserved
objects: Sketcher::SketchObject×9, PartDesign::Pad×6, App::Point×5, PartDesign::Body×4, App::Link×4, App::FeaturePython×4, PartDesign::ShapeBinder×2, PartDesign::Plane×2, PartDesign::Fillet×2, PartDesign::Chamfer×1, PartDesign::Hole×1, PartDesign::AdditiveHelix×1, PartDesign::Pocket×1, PartDesign::Mirrored×1, PartDesign::SubtractiveHelix×1, PartDesign::PolarPattern×1, Assembly::JointGroup×1, Assembly::AssemblyObject×1
note: 69 computed .brp shape members not serialized (recipe doc carries the construction recipe); baked Part::Feature solids carry a one-line shape summary decoded from their .brp

FEATURE [App::Point] Origin001
  Role = Origin
FEATURE [Sketcher::SketchObject] Sketch
  ArcFitTolerance = 1e-06
  AttachmentSupport = -> [Origin]
  ExternalTypes = [0]
  FullyConstrained = true
  MakeInternals = false
  MapMode = 5
  Placement = pos=(0,0,0) rot=(1,0,0;1.5708rad)
  _ExternalGeoVersion = 1
  sketch-geometry (1):
    g0: Circle CenterX=0 CenterY=0 CenterZ=0 NormalX=0 NormalY=0 NormalZ=1 AngleXU=0 Radius=6
  constraints (2):
    c: Diameter(g0) = 12
    c: Coincident(g0,g-1)
FEATURE [PartDesign::Pad] Pad
  Direction = (0,-1,2e-16)
  Length = 18
  Length2 = 10
  Profile = -> Sketch
  ReferenceAxis = -> Sketch [N_Axis]
  Refine = true
  SideType = 0
  Suppressed = false
  Type = 0
  Type2 = 0
FEATURE [Sketcher::SketchObject] Sketch001
  ArcFitTolerance = 1e-06
  AttachmentSupport = -> [Pad]
  ExternalTypes = [0]
  FullyConstrained = true
  MakeInternals = false
  MapMode = 5
  Placement = pos=(0,-18,0) rot=(1,0,0;1.5708rad)
  _ExternalGeoVersion = 1
  sketch-geometry (1):
    g0: Circle CenterX=0 CenterY=0 CenterZ=0 NormalX=0 NormalY=0 NormalZ=1 AngleXU=0 Radius=7
  constraints (2):
    c: Diameter(g0) = 14
    c: Coincident(g0,g-1)
FEATURE [PartDesign::Pad] Pad001
  BaseFeature = -> Pad
  Direction = (0,-1,2e-16)
  Length = 2
  Length2 = 10
  Profile = -> Sketch001
  ReferenceAxis = -> Sketch001 [N_Axis]
  Refine = true
  SideType = 0
  Suppressed = false
  Type = 0
  Type2 = 0
FEATURE [PartDesign::Chamfer] Chamfer
  Angle = 45
  Base = -> Pad001 [Edge6]
  BaseFeature = -> Pad001
  ChamferType = 0
  FlipDirection = false
  Refine = true
  Size = 1
  Size2 = 1
  SupportTransform = false
  Suppressed = false
  UseAllEdges = false
FEATURE [PartDesign::Hole] Hole
  BaseFeature = -> Chamfer
  BaseProfileType = 7
  CustomThreadClearance = 0
  Depth = 6
  DepthType = 0
  Diameter = 9.1
  DrillForDepth = false
  DrillPoint = 0
  DrillPointAngle = 118
  HoleCutCountersinkAngle = 90
  HoleCutCustomValues = false
  HoleCutDepth = 0
  HoleCutDiameter = 0
  HoleCutType = 0
  ModelThread = false
  Profile = -> Chamfer [Face4]
  Refine = true
  Suppressed = false
  Tapered = false
  TaperedAngle = 90
  ThreadClass = 0
  ThreadDepth = 6
  ThreadDepthType = 0
  ThreadDiameter = 9.1
  ThreadDirection = 0
  ThreadFit = 0
  ThreadSize = 0
  ThreadType = 0
  Threaded = false
  UseCustomThreadClearance = false
FEATURE [Sketcher::SketchObject] Sketch004
  ArcFitTolerance = 1e-06
  AttachmentSupport = -> [Origin]
  ExternalTypes = [0]
  FullyConstrained = true
  MakeInternals = false
  MapMode = 5
  _ExternalGeoVersion = 1
  sketch-geometry (4):
    g0: LineSegment StartX=6 StartY=-18 StartZ=0 EndX=6.25 EndY=-18 EndZ=0
    g1: LineSegment StartX=6.25 StartY=-18 StartZ=0 EndX=6.25 EndY=-17.75 EndZ=0
    g2: LineSegment StartX=6.25 StartY=-17.75 StartZ=0 EndX=6 EndY=-17.75 EndZ=0
    g3: LineSegment StartX=6 StartY=-17.75 StartZ=0 EndX=6 EndY=-18 EndZ=0
  constraints (11):
    c: Coincident(g0,g-3)
    c: Horizontal(g0)
    c: Coincident(g1,g0)
    c: Vertical(g1)
    c: Coincident(g2,g1)
    c: PointOnObject(g2,g-3)
    c: Horizontal(g2)
    c: DistanceY(g1,g1) = 0.25
    c: DistanceX(g2,g2) = 0.25
    c: Coincident(g3,g2)
    c: Coincident(g3,g0)
FEATURE [PartDesign::AdditiveHelix] AdditiveHelix
  Angle = 0
  Axis = (0,1,0)
  Base = (0,0,0)
  BaseFeature = -> Hole
  Growth = 0
  HasBeenEdited = true
  Height = 9
  LeftHanded = false
  Mode = 0
  Outside = false
  Pitch = 0.388909
  Profile = -> Sketch004
  ReferenceAxis = -> Sketch004 [V_Axis]
  Refine = true
  Suppressed = false
  Tolerance = 0.1
  Turns = 23.1417
FEATURE [PartDesign::Body] Body  label="base"
  AllowCompound = true
  Group = -> [Sketch,Pad,Sketch001,Pad001,Chamfer,Hole,Sketch004,AdditiveHelix]
  Origin = -> Origin
  Tip = -> AdditiveHelix
FEATURE [App::Point] Origin003
  Role = Origin
FEATURE [PartDesign::ShapeBinder] CopyAdditiveHelix
  TraceSupport = false
FEATURE [PartDesign::Plane] DatumPlane
  AttachmentSupport = -> [CopyAdditiveHelix]
  Length = 60
  MapMode = 5
  Placement = pos=(0,0,0) rot=(0,0.707107,0.707107;3.14159rad)
  ResizeMode = 0
  Width = 60
FEATURE [Sketcher::SketchObject] Sketch005
  ArcFitTolerance = 1e-06
  AttachmentSupport = -> [DatumPlane]
  ExternalGeometry = -> [CopyAdditiveHelix]
  ExternalTypes = [0]
  FullyConstrained = true
  MakeInternals = false
  MapMode = 5
  Placement = pos=(0,0,0) rot=(0,0.707107,0.707107;3.14159rad)
  _ExternalGeoVersion = 1
  sketch-geometry (4):
    g0: LineSegment StartX=4 StartY=0 StartZ=0 EndX=4.5 EndY=0 EndZ=0
    g1: LineSegment StartX=4.5 StartY=0 StartZ=0 EndX=4.5 EndY=-2 EndZ=0
    g2: LineSegment StartX=4.5 StartY=-2 StartZ=0 EndX=4 EndY=-2 EndZ=0
    g3: LineSegment StartX=4 StartY=-2 StartZ=0 EndX=4 EndY=0 EndZ=0
  constraints (12):
    c: Coincident(g0,g1)
    c: Coincident(g1,g2)
    c: Coincident(g2,g3)
    c: Coincident(g3,g0)
    c: Horizontal(g0)
    c: Horizontal(g2)
    c: Vertical(g1)
    c: Vertical(g3)
    c: Distance(g1,g3) = 0.5
    c: Distance(g0,g2) = 2
    c: PointOnObject(g0,g-1)
    c: Distance(g-3,g3) = 2
FEATURE [PartDesign::Pad] Pad002
  Direction = (0,1,-2e-16)
  Length = 5
  Length2 = 10
  Placement = pos=(0,0,0) rot=(0,0.707107,0.707107;3.14159rad)
  Profile = -> Sketch005
  ReferenceAxis = -> Sketch005 [N_Axis]
  Refine = true
  SideType = 0
  Suppressed = false
  Type = 0
  Type2 = 0
FEATURE [Sketcher::SketchObject] Sketch006
  ArcFitTolerance = 1e-06
  AttachmentSupport = -> [Pad002]
  ExternalTypes = [0]
  FullyConstrained = true
  MakeInternals = false
  MapMode = 5
  Placement = pos=(-4.5,-4e-16,4e-16) rot=(0,-1,0;1.5708rad)
  _ExternalGeoVersion = 1
  sketch-geometry (4):
    g0: LineSegment StartX=-1.5 StartY=4 StartZ=0 EndX=-1.5 EndY=2 EndZ=0
    g1: LineSegment StartX=-1.5 StartY=2 StartZ=0 EndX=-0.5 EndY=2 EndZ=0
    g2: LineSegment StartX=-0.5 StartY=2 StartZ=0 EndX=-0.5 EndY=4 EndZ=0
    g3: LineSegment StartX=-0.5 StartY=4 StartZ=0 EndX=-1.5 EndY=4 EndZ=0
  constraints (12):
    c: Coincident(g0,g1)
    c: Coincident(g1,g2)
    c: Coincident(g2,g3)
    c: Coincident(g3,g0)
    c: Vertical(g0)
    c: Vertical(g2)
    c: Horizontal(g1)
    c: Horizontal(g3)
    c: DistanceY(g2,g2) = 2
    c: DistanceX(g3,g3) = 1
    c: Distance(g-2,g2) = 0.5
    c: Distance(g-1,g1) = 2
FEATURE [PartDesign::Pocket] Pocket
  BaseFeature = -> Pad002
  Direction = (1,0,-2e-16)
  Length = 5
  Length2 = 5
  Placement = pos=(0,0,0) rot=(0,0.707107,0.707107;3.14159rad)
  Profile = -> Sketch006
  ReferenceAxis = -> Sketch006 [N_Axis]
  Refine = true
  SideType = 0
  Suppressed = false
  Type = 1
  Type2 = 0
FEATURE [PartDesign::Mirrored] Mirrored
  BaseFeature = -> Pocket
  MirrorPlane = -> YZ_Plane001
  Originals = -> [Pad002,Pocket]
  Placement = pos=(0,0,0) rot=(0,0.707107,0.707107;3.14159rad)
  Refine = true
  Suppressed = false
  TransformMode = 0
FEATURE [PartDesign::Body] Body001  label="pins"
  AllowCompound = true
  Group = -> [DatumPlane,CopyAdditiveHelix,Sketch005,Pad002,Sketch006,Pocket,Mirrored]
  Origin = -> Origin002
  Tip = -> Mirrored
FEATURE [App::Point] Origin005  label="Origin006"
  Role = Origin
FEATURE [PartDesign::ShapeBinder] CopyAdditiveHelix001
  Placement = pos=(0,-20,0) rot=(0,0,1;0rad)
  TraceSupport = false
FEATURE [PartDesign::Plane] DatumPlane001
  AttachmentSupport = -> [CopyAdditiveHelix001]
  Length = 60
  MapMode = 11
  Placement = pos=(0,-20,0) rot=(0.57735,0.57735,-0.57735;2.0944rad)
  ResizeMode = 0
  Width = 60
FEATURE [Sketcher::SketchObject] Sketch007
  ArcFitTolerance = 1e-06
  AttachmentSupport = -> [DatumPlane001]
  ExternalTypes = [0]
  FullyConstrained = true
  MakeInternals = false
  MapMode = 5
  Placement = pos=(0,-20,0) rot=(0.57735,0.57735,-0.57735;2.0944rad)
  _ExternalGeoVersion = 1
  sketch-geometry (1):
    g0: Circle CenterX=0 CenterY=0 CenterZ=0 NormalX=0 NormalY=0 NormalZ=1 AngleXU=0 Radius=4.5
  constraints (2):
    c: Diameter(g0) = 9
    c: Coincident(g0,g-1)
FEATURE [PartDesign::Pad] Pad003
  Direction = (0,-1,0)
  Length = 4
  Length2 = 10
  Placement = pos=(0,-20,0) rot=(0.57735,0.57735,-0.57735;2.0944rad)
  Profile = -> Sketch007
  ReferenceAxis = -> Sketch007 [N_Axis]
  Refine = true
  SideType = 0
  Suppressed = false
  Type = 0
  Type2 = 0
FEATURE [PartDesign::Fillet] Fillet
  Base = -> Pad003 [Edge3]
  BaseFeature = -> Pad003
  Placement = pos=(0,-20,0) rot=(0.57735,0.57735,-0.57735;2.0944rad)
  Radius = 1
  Refine = true
  SupportTransform = false
  Suppressed = false
  UseAllEdges = false
FEATURE [PartDesign::Body] Body002  label="button"
  AllowCompound = true
  Group = -> [DatumPlane001,CopyAdditiveHelix001,Sketch007,Pad003,Fillet]
  Origin = -> Origin004
  Tip = -> Fillet
FEATURE [App::Point] Origin007  label="Origin009"
  Role = Origin
FEATURE [Sketcher::SketchObject] Sketch008
  ArcFitTolerance = 1e-06
  AttachmentSupport = -> [Origin006]
  ExternalTypes = [0]
  FullyConstrained = true
  MakeInternals = false
  MapMode = 5
  Placement = pos=(0,0,0) rot=(1,0,0;1.5708rad)
  _ExternalGeoVersion = 1
  sketch-geometry (2):
    g0: Circle CenterX=0 CenterY=0 CenterZ=0 NormalX=0 NormalY=0 NormalZ=1 AngleXU=0 Radius=8
    g1: Circle CenterX=0 CenterY=0 CenterZ=0 NormalX=0 NormalY=0 NormalZ=1 AngleXU=0 Radius=6.5
  constraints (4):
    c: Diameter(g0) = 16
    c: Coincident(g0,g-1)
    c: Diameter(g1) = 13
    c: Coincident(g1,g0)
FEATURE [PartDesign::Pad] Pad004
  Direction = (0,-1,2e-16)
  Length = 2
  Length2 = 10
  Profile = -> Sketch008
  ReferenceAxis = -> Sketch008 [N_Axis]
  Refine = true
  SideType = 0
  Suppressed = false
  Type = 0
  Type2 = 0
FEATURE [Sketcher::SketchObject] Sketch009
  ArcFitTolerance = 1e-06
  AttachmentSupport = -> [Origin006]
  ExternalGeometry = -> [Pad004]
  ExternalTypes = [0,0]
  FullyConstrained = true
  MakeInternals = false
  MapMode = 5
  _ExternalGeoVersion = 1
  sketch-geometry (4):
    g0: LineSegment StartX=6.5 StartY=-2 StartZ=0 EndX=8 EndY=-2 EndZ=0
    g1: LineSegment StartX=8 StartY=-2 StartZ=0 EndX=8 EndY=-1 EndZ=0
    g2: LineSegment StartX=8 StartY=-1 StartZ=0 EndX=6.5 EndY=-1 EndZ=0
    g3: LineSegment StartX=6.5 StartY=-1 StartZ=0 EndX=6.5 EndY=-2 EndZ=0
  constraints (11):
    c: Coincident(g0,g1)
    c: Coincident(g1,g2)
    c: Coincident(g2,g3)
    c: Coincident(g3,g0)
    c: Horizontal(g0)
    c: Horizontal(g2)
    c: Vertical(g1)
    c: Vertical(g3)
    c: Coincident(g0,g-4)
    c: PointOnObject(g1,g-3)
    c: DistanceY(g1,g1) = 1
FEATURE [PartDesign::SubtractiveHelix] SubtractiveHelix
  Angle = 0
  Axis = (0,1,0)
  Base = (0,0,0)
  BaseFeature = -> Pad004
  Growth = 0
  HasBeenEdited = true
  Height = 1
  LeftHanded = false
  Mode = 0
  Outside = false
  Pitch = 8
  Profile = -> Sketch009
  ReferenceAxis = -> Sketch009 [V_Axis]
  Refine = true
  Reversed = true
  Suppressed = false
  Tolerance = 0.1
  Turns = 0.125
FEATURE [PartDesign::PolarPattern] PolarPattern
  Angle = 360
  Axis = -> Y_Axis003
  BaseFeature = -> SubtractiveHelix
  Mode = 0
  Occurrences = 8
  Offset = 120
  Originals = -> [SubtractiveHelix]
  Refine = true
  SpacingPattern = [0]
  Spacings = [-1,-1,-1,-1,-1,-1,-1]
  Suppressed = false
  TransformMode = 0
FEATURE [Sketcher::SketchObject] Sketch010
  ArcFitTolerance = 1e-06
  AttachmentSupport = -> [PolarPattern]
  ExternalGeometry = -> [PolarPattern]
  ExternalTypes = [0]
  FullyConstrained = false
  MakeInternals = false
  MapMode = 5
  Placement = pos=(0,0,0) rot=(0,0.707107,0.707107;3.14159rad)
  _ExternalGeoVersion = 1
  sketch-geometry (14):
    g0: LineSegment StartX=0.0147037 StartY=7.99999 StartZ=0 EndX=-6.92084 EndY=4.01273 EndZ=0
    g1: LineSegment StartX=-6.92084 StartY=4.01273 StartZ=0 EndX=-6.93554 EndY=-3.98726 EndZ=0
    g2: LineSegment StartX=-6.93554 StartY=-3.98726 StartZ=0 EndX=-0.0147037 EndY=-7.99999 EndZ=0
    g3: LineSegment StartX=-0.0147037 StartY=-7.99999 StartZ=0 EndX=6.92084 EndY=-4.01273 EndZ=0
    g4: LineSegment StartX=6.92084 StartY=-4.01273 StartZ=0 EndX=6.93554 EndY=3.98726 EndZ=0
    g5: LineSegment StartX=6.93554 StartY=3.98726 StartZ=0 EndX=0.0147037 EndY=7.99999 EndZ=0
    g6: Circle [constr] CenterX=0 CenterY=0 CenterZ=0 NormalX=0 NormalY=0 NormalZ=1 AngleXU=0 Radius=8
    g7: LineSegment StartX=0 StartY=6.99999 StartZ=0 EndX=-6.06217 EndY=3.49999 EndZ=0
    g8: LineSegment StartX=-6.06217 StartY=3.49999 StartZ=0 EndX=-6.06217 EndY=-3.49999 EndZ=0
    g9: LineSegment StartX=-6.06217 StartY=-3.49999 StartZ=0 EndX=9e-16 EndY=-6.99999 EndZ=0
    g10: LineSegment StartX=9e-16 StartY=-6.99999 StartZ=0 EndX=6.06217 EndY=-3.49999 EndZ=0
    g11: LineSegment StartX=6.06217 StartY=-3.49999 StartZ=0 EndX=6.06217 EndY=3.49999 EndZ=0
    g12: LineSegment StartX=6.06217 StartY=3.49999 StartZ=0 EndX=0 EndY=6.99999 EndZ=0
    g13: Circle [constr] CenterX=0 CenterY=0 CenterZ=0 NormalX=0 NormalY=0 NormalZ=1 AngleXU=0 Radius=6.99999
  constraints (31):
    c: Coincident(g0,g1)
    c: Coincident(g1,g2)
    c: Coincident(g2,g3)
    c: Coincident(g3,g4)
    c: Coincident(g4,g5)
    c: Coincident(g5,g0)
    c: Equal(g0, g1-g5) x5
    c: PointOnObject(g0,g6)
    c: PointOnObject(g1,g6)
    c: PointOnObject(g2,g6)
    c: PointOnObject(g3,g6)
    c: PointOnObject(g4,g6)
    c: PointOnObject(g5,g6)
    c: Coincident(g6,g-3)
    c: PointOnObject(g5,g-3)
    c: Coincident(g7,g8)
    c: Coincident(g8,g9)
    c: Coincident(g9,g10)
    c: Coincident(g10,g11)
    c: Coincident(g11,g12)
    c: Coincident(g12,g7)
    c: Equal(g7, g8-g12) x5
    c: PointOnObject(g7,g13)
    c: PointOnObject(g8,g13)
    c: PointOnObject(g9,g13)
    c: PointOnObject(g10,g13)
    c: PointOnObject(g11,g13)
    c: PointOnObject(g12,g13)
    c: Coincident(g13,g6)
    c: PointOnObject(g12,g-2)
    c: DistanceY(g7,g0) = 1
FEATURE [PartDesign::Pad] Pad005
  BaseFeature = -> PolarPattern
  Direction = (0,1,-2e-16)
  Length = 3
  Length2 = 10
  Profile = -> Sketch010
  ReferenceAxis = -> Sketch010 [N_Axis]
  Refine = true
  SideType = 0
  Suppressed = false
  Type = 0
  Type2 = 0
FEATURE [PartDesign::Fillet] Fillet001
  Base = -> Pad005 [Edge113,Edge118,Edge117,Edge114,Edge116,Edge115]
  BaseFeature = -> Pad005
  Radius = 2
  Refine = true
  SupportTransform = false
  Suppressed = false
  UseAllEdges = false
FEATURE [PartDesign::Body] Body003  label="nut"
  AllowCompound = true
  Group = -> [Sketch008,Pad004,Sketch009,SubtractiveHelix,PolarPattern,Sketch010,Pad005,Fillet001]
  Origin = -> Origin006
  Placement = pos=(0,-14,0) rot=(0,0,1;0rad)
  Tip = -> Fillet001
FEATURE [App::Point] Origin009  label="Origin011"
  Role = Origin
FEATURE [App::Link] base  label="base001"
  LinkedObject = -> Body
FEATURE [App::FeaturePython] GroundedJoint  # Assembly grounded joint (typed FeaturePython)
  ObjectToGround = -> base
FEATURE [App::Link] pins  label="pins001"
  LinkPlacement = pos=(-0.25,7e-16,1) rot=(0,0,1;0rad)
  LinkedObject = -> Body001
  Placement = pos=(-0.25,7e-16,1) rot=(0,0,1;0rad)
FEATURE [App::Link] nut  label="nut001"
  LinkPlacement = pos=(0,-11.7053,2.6e-15) rot=(0,0,1;0rad)
  LinkedObject = -> Body003
  Placement = pos=(0,-11.7053,2.6e-15) rot=(0,0,1;0rad)
FEATURE [App::Link] button  label="button001"
  LinkPlacement = pos=(-4.8e-15,1.5,-4.6e-15) rot=(0,1,0;1.5708rad)
  LinkedObject = -> Body002
  Placement = pos=(-4.8e-15,1.5,-4.6e-15) rot=(0,1,0;1.5708rad)
FEATURE [App::FeaturePython] Joint  label="Slider004"  # Assembly joint (typed FeaturePython)
  Angle = 0
  AngleMax = 0
  AngleMin = 0
  Detach1 = false
  Detach2 = false
  Distance = 0
  Distance2 = 0
  EnableAngleMax = false
  EnableAngleMin = false
  EnableLengthMax = false
  EnableLengthMin = false
  JointType = 3 (Slider)
  LengthMax = 0
  LengthMin = 0
  Placement1 = pos=(2e-16,-21.5,0) rot=(0.57735,0.57735,-0.57735;2.0944rad)
  Placement2 = pos=(0,-20,0) rot=(0,-0.707107,0.707107;3.14159rad)
  Reference1 = -> button [Face1,Face1]
  Reference2 = -> base [Edge50,Edge50]
  Suppressed = false
FEATURE [App::FeaturePython] Joint001  label="Fixed"  # Assembly joint (typed FeaturePython)
  Angle = 0
  AngleMax = 0
  AngleMin = 0
  Detach1 = false
  Detach2 = false
  Distance = 0
  Distance2 = 0
  EnableAngleMax = false
  EnableAngleMin = false
  EnableLengthMax = false
  EnableLengthMin = false
  JointType = 0 (Fixed)
  LengthMax = 0
  LengthMin = 0
  Offset1 = pos=(0,4,0) rot=(0,0,1;0rad)
  Placement1 = pos=(0.25,-2e-16,-1) rot=(-0.57735,0.57735,-0.57735;4.18879rad)
  Placement2 = pos=(0,0,1e-16) rot=(0.57735,0.57735,0.57735;4.18879rad)
  Reference1 = -> pins [Face14,Face14]
  Reference2 = -> base [Face105,Face105]
  Suppressed = false
FEATURE [App::FeaturePython] Joint002  label="Revolute004"  # Assembly joint (typed FeaturePython)
  Angle = 0
  AngleMax = 0
  AngleMin = 0
  Detach1 = false
  Detach2 = false
  Distance = 0
  Distance2 = 0
  EnableAngleMax = false
  EnableAngleMin = false
  EnableLengthMax = false
  EnableLengthMin = false
  JointType = 1 (Revolute)
  LengthMax = 0
  LengthMin = 0
  Offset2 = pos=(0,0,8) rot=(0,0,1;0rad)
  Placement1 = pos=(0,-0.777778,2e-16) rot=(1,0,0;1.5708rad)
  Placement2 = pos=(0,-12.4831,2.8e-15) rot=(1,0,0;1.5708rad)
  Reference1 = -> nut [Fillet001.Face38,Fillet001.Face38]
  Reference2 = -> base [AdditiveHelix.Face101,AdditiveHelix.Face101]
  Suppressed = false
FEATURE [Assembly::JointGroup] Joints
  Group = -> [GroundedJoint,Joint,Joint001,Joint002]
FEATURE [Assembly::AssemblyObject] Assembly
  Group = -> [Joints,base,GroundedJoint,pins,nut,button,Joint,Joint001,Joint002]
  Origin = -> Origin008
  Type = Assembly
---- part housing.FCStd = doc fcstd_e9bb2e9295da ----
FCSTD DOCUMENT  (FreeCAD 1.1R20260414 (Git shallow))
Label: housing
License: All rights reserved
LicenseURL: https://en.wikipedia.org/wiki/All_rights_reserved
objects: Sketcher::SketchObject×5, PartDesign::Pocket×3, PartDesign::Pad×2, App::Point×1, PartDesign::Fillet×1, PartDesign::Body×1
note: 29 computed .brp shape members not serialized (recipe doc carries the construction recipe); baked Part::Feature solids carry a one-line shape summary decoded from their .brp

FEATURE [App::Point] Origin005  label="Origin006"
  Role = Origin
FEATURE [Sketcher::SketchObject] Sketch
  ArcFitTolerance = 1e-06
  AttachmentSupport = -> [Origin004]
  ExternalTypes = [0]
  FullyConstrained = true
  MakeInternals = false
  MapMode = 5
  Placement = pos=(0,0,0) rot=(1,0,0;1.5708rad)
  _ExternalGeoVersion = 1
  sketch-geometry (10):
    g0: LineSegment StartX=-40 StartY=-60 StartZ=0 EndX=40 EndY=-60 EndZ=0
    g1: LineSegment StartX=45 StartY=-55 StartZ=0 EndX=45 EndY=55 EndZ=0
    g2: LineSegment StartX=40 StartY=60 StartZ=0 EndX=-40 EndY=60 EndZ=0
    g3: LineSegment StartX=-45 StartY=55 StartZ=0 EndX=-45 EndY=-55 EndZ=0
    g4: ArcOfCircle CenterX=-40 CenterY=-55 CenterZ=0 NormalX=0 NormalY=0 NormalZ=1 AngleXU=0 Radius=5 StartAngle=3.14159 EndAngle=4.71239
    g5: ArcOfCircle CenterX=40 CenterY=-55 CenterZ=0 NormalX=0 NormalY=0 NormalZ=1 AngleXU=0 Radius=5 StartAngle=4.71239 EndAngle=6.28319
    g6: ArcOfCircle CenterX=40 CenterY=55 CenterZ=0 NormalX=0 NormalY=0 NormalZ=1 AngleXU=0 Radius=5 StartAngle=0 EndAngle=1.5708
    g7: ArcOfCircle CenterX=-40 CenterY=55 CenterZ=0 NormalX=0 NormalY=0 NormalZ=1 AngleXU=0 Radius=5 StartAngle=1.5708 EndAngle=3.14159
    g8: GeomPoint [constr] X=45 Y=60 Z=0
    g9: GeomPoint [constr] X=0 Y=0 Z=0
  constraints (22):
    c: Tangent(g0,g4) = -1.5708
    c: Tangent(g0,g5) = -1.5708
    c: Tangent(g1,g5) = -1.5708
    c: Tangent(g1,g6) = -1.5708
    c: Tangent(g2,g6) = -1.5708
    c: Tangent(g2,g7) = -1.5708
    c: Tangent(g3,g7) = -1.5708
    c: Tangent(g3,g4) = -1.5708
    c: Horizontal(g0)
    c: Horizontal(g2)
    c: Vertical(g1)
    c: Vertical(g3)
    c: Equal(g4,g5)
    c: Equal(g5,g6)
    c: Equal(g6,g7)
    c: Symmetric(g2,g0,g9)
    c: PointOnObject(g8,g1)
    c: PointOnObject(g8,g2)
    c: Distance(g1,g3) = 90
    c: Distance(g0,g2) = 120
    c: Radius(g5) = 5
    c: Coincident(g9,g-1)
FEATURE [PartDesign::Pad] Pad
  Direction = (0,-1,2e-16)
  Length = 120
  Length2 = 10
  Profile = -> Sketch
  ReferenceAxis = -> Sketch [N_Axis]
  Refine = true
  SideType = 0
  Suppressed = false
  Type = 0
  Type2 = 0
FEATURE [Sketcher::SketchObject] Sketch001
  ArcFitTolerance = 1e-06
  AttachmentSupport = -> [Pad]
  ExternalGeometry = -> [Pad]
  ExternalTypes = [0,0]
  FullyConstrained = false
  MakeInternals = false
  MapMode = 5
  Placement = pos=(0,-120,0) rot=(1,0,0;1.5708rad)
  _ExternalGeoVersion = 1
  sketch-geometry (8):
    g0: LineSegment StartX=-39.8496 StartY=-59.5 StartZ=0 EndX=40.0299 EndY=-59.5 EndZ=0
    g1: ArcOfCircle CenterX=40.0299 CenterY=-55.0299 CenterZ=0 NormalX=0 NormalY=0 NormalZ=1 AngleXU=0 Radius=4.47014 StartAngle=4.71239 EndAngle=6.28319
    g2: LineSegment StartX=44.5 StartY=-55.0299 StartZ=0 EndX=44.5 EndY=55.1148 EndZ=0
    g3: ArcOfCircle CenterX=40.1148 CenterY=55.1148 CenterZ=0 NormalX=0 NormalY=0 NormalZ=1 AngleXU=0 Radius=4.38516 StartAngle=7e-16 EndAngle=1.5708
    g4: LineSegment StartX=40.1148 StartY=59.5 StartZ=0 EndX=-39.6831 EndY=59.5 EndZ=0
    g5: ArcOfCircle CenterX=-39.6831 CenterY=54.6831 CenterZ=0 NormalX=0 NormalY=0 NormalZ=1 AngleXU=0 Radius=4.81689 StartAngle=1.5708 EndAngle=3.14159
    g6: LineSegment StartX=-44.5 StartY=54.6831 StartZ=0 EndX=-44.5 EndY=-54.8496 EndZ=0
    g7: ArcOfCircle CenterX=-39.8496 CenterY=-54.8496 CenterZ=0 NormalX=0 NormalY=0 NormalZ=1 AngleXU=0 Radius=4.65041 StartAngle=3.14159 EndAngle=4.71239
  constraints (16):
    c: Tangent(g0,g1) = -1.5708
    c: Tangent(g0,g7) = -1.5708
    c: Tangent(g1,g2) = -1.5708
    c: Tangent(g2,g3) = -1.5708
    c: Tangent(g3,g4) = -1.5708
    c: Tangent(g4,g5) = -1.5708
    c: Tangent(g5,g6) = -1.5708
    c: Tangent(g6,g7) = -1.5708
    c: Horizontal(g4)
    c: Vertical(g2)
    c: Vertical(g6)
    c: Horizontal(g0)
    c: Distance(g-8,g4) = 0.5
    c: Distance(g-10,g6) = 0.5
    c: Distance(g-6,g2) = 0.5
    c: Distance(g0,g-4) = 0.5
FEATURE [PartDesign::Pocket] Pocket
  BaseFeature = -> Pad
  Direction = (0,1,-2e-16)
  Length = 118
  Length2 = 5
  Profile = -> Sketch001
  ReferenceAxis = -> Sketch001 [N_Axis]
  Refine = true
  SideType = 0
  Suppressed = false
  Type = 0
  Type2 = 0
FEATURE [Sketcher::SketchObject] Sketch002
  ArcFitTolerance = 1e-06
  AttachmentSupport = -> [Pocket]
  ExternalGeometry = -> [Pocket]
  ExternalTypes = [0]
  FullyConstrained = true
  MakeInternals = false
  MapMode = 5
  Placement = pos=(0,0,0) rot=(0,0.707107,0.707107;3.14159rad)
  _ExternalGeoVersion = 1
  sketch-geometry (1):
    g0: Circle CenterX=0 CenterY=39.75 CenterZ=0 NormalX=0 NormalY=0 NormalZ=1 AngleXU=0 Radius=5.25
  constraints (3):
    c: Diameter(g0) = 10.5
    c: PointOnObject(g0,g-2)
    c: Distance(g0,g-3) = 15
FEATURE [PartDesign::Pocket] Pocket001
  BaseFeature = -> Pocket
  Direction = (0,-1,2e-16)
  Length = 5
  Length2 = 5
  Profile = -> Sketch002
  ReferenceAxis = -> Sketch002 [N_Axis]
  Refine = true
  SideType = 0
  Suppressed = false
  Type = 0
  Type2 = 0
FEATURE [Sketcher::SketchObject] Sketch003
  ArcFitTolerance = 1e-06
  AttachmentSupport = -> [Pocket001]
  ExternalGeometry = -> [Pocket001]
  ExternalTypes = [0,0]
  FullyConstrained = true
  MakeInternals = false
  MapMode = 5
  Placement = pos=(0,-2,5e-16) rot=(1,0,0;1.5708rad)
  _ExternalGeoVersion = 1
  sketch-geometry (4):
    g0: ArcOfCircle CenterX=0 CenterY=39.75 CenterZ=0 NormalX=0 NormalY=0 NormalZ=1 AngleXU=0 Radius=7.25 StartAngle=2.97339 EndAngle=6.45139
    g1: LineSegment StartX=-7.14768 StartY=40.9638 StartZ=0 EndX=-4 EndY=59.5 EndZ=0
    g2: LineSegment StartX=7.14768 StartY=40.9638 StartZ=0 EndX=4 EndY=59.5 EndZ=0
    g3: LineSegment StartX=4 StartY=59.5 StartZ=0 EndX=-4 EndY=59.5 EndZ=0
  constraints (10):
    c: PointOnObject(g1,g-4)
    c: Coincident(g0,g-3)
    c: PointOnObject(g2,g-4)
    c: Tangent(g1,g0) = 1.5708
    c: Coincident(g3,g2)
    c: Coincident(g3,g1)
    c: Tangent(g0,g2) = -1.5708
    c: Distance(g-3,g0) = 2
    c: Distance(g2,g-2) = 4
    c: Distance(g1,g-2) = 4
FEATURE [PartDesign::Pad] Pad001
  BaseFeature = -> Pocket001
  Direction = (0,-1,2e-16)
  Length = 20
  Length2 = 10
  Profile = -> Sketch003
  ReferenceAxis = -> Sketch003 [N_Axis]
  Refine = true
  SideType = 0
  Suppressed = false
  Type = 0
  Type2 = 0
FEATURE [PartDesign::Fillet] Fillet
  Base = -> Pad001 [Edge56,Edge55,Edge42,Edge54,Edge44]
  BaseFeature = -> Pad001
  Radius = 1
  Refine = true
  SupportTransform = false
  Suppressed = false
  UseAllEdges = false
FEATURE [Sketcher::SketchObject] Sketch004
  ArcFitTolerance = 1e-06
  AttachmentSupport = -> [Fillet]
  ExternalGeometry = -> [Fillet]
  ExternalTypes = [0]
  FullyConstrained = true
  MakeInternals = false
  MapMode = 5
  Placement = pos=(-45,0,0) rot=(0.57735,-0.57735,-0.57735;2.0944rad)
  _ExternalGeoVersion = 1
  sketch-geometry (4):
    g0: LineSegment StartX=0 StartY=-37.5 StartZ=0 EndX=-12.9904 EndY=-60 EndZ=0
    g1: LineSegment StartX=-12.9904 StartY=-60 StartZ=0 EndX=12.9904 EndY=-60 EndZ=0
    g2: LineSegment StartX=12.9904 StartY=-60 StartZ=0 EndX=0 EndY=-37.5 EndZ=0
    g3: Circle [constr] CenterX=7.676e-13 CenterY=-52.5 CenterZ=0 NormalX=0 NormalY=0 NormalZ=1 AngleXU=0 Radius=15
  constraints (12):
    c: Coincident(g0,g1)
    c: Coincident(g1,g2)
    c: Coincident(g2,g0)
    c: Equal(g0,g1)
    c: Equal(g0,g2)
    c: PointOnObject(g0,g3)
    c: PointOnObject(g1,g3)
    c: PointOnObject(g2,g3)
    c: Radius(g3) = 15
    c: PointOnObject(g0,g-2)
    c: PointOnObject(g1,g-4)
    c: Horizontal(g1)
FEATURE [PartDesign::Pocket] Pocket002
  BaseFeature = -> Fillet
  Direction = (1,0,0)
  Length = 5
  Length2 = 5
  Profile = -> Sketch004
  ReferenceAxis = -> Sketch004 [N_Axis]
  Refine = true
  SideType = 0
  Suppressed = false
  Type = 1
  Type2 = 0
FEATURE [PartDesign::Body] Body001  label="housing"
  AllowCompound = true
  Group = -> [Sketch,Pad,Sketch001,Pocket,Sketch002,Pocket001,Sketch003,Pad001,Fillet,Sketch004,Pocket002]
  Origin = -> Origin004
  Tip = -> Pocket002
